# Revit family: ERA_LF_WC_SPB-201
name_source: partatom
category: Осветительные приборы
units: mm (PartAtom-declared; Revit-internal decimal feet)

## family parameters
Всегда вертикально = Да
Заголовок OmniClass = Lighting
Источник света = Да
На основе рабочей плоскости = Нет
Номер OmniClass = 23.80.70.00
Общий = Нет
При загрузке вырезать с полостями = Нет
Размер круглого соединителя = Использовать диаметр
Тип детали = Нормальный
Точка расчета площади = Да

## types (16) — shared parameters
ADSK_Единица измерения = шт.
ADSK_Завод-изготовитель = ЭРА
ADSK_Классификация нагрузок = Освещение
ADSK_Количество фаз = 1
ADSK_Наименование краткое = Светильник
ADSK_Напряжение = 230 В
ADSK_Примечание = Импульсный драйвер
URL = https://www.eraworld.ru
_Корпус_Длина = 1 мм
_Корпус_Ширина = 1 мм
_УГО_Диаметр = 1 мм
_УГО_Длина = 1 мм
_УГО_Ширина = 1 мм
Видимая форма излучения при визуализации = Нет
Геометрия изделия = Круглый
Излучение по длине прямоугольника = 1 мм
Излучение по ширине прямоугольника = 1 мм
Источник света = LED
Класс защиты = II
Класс пожароопасности = Нет
Комплект = Импульсный драйвер
Разработчик модели = https://www.teslabim.ru
Светофильтр = 16777215
Смещение цветовой температуры при затухании лампы = <Нет>
Степень защиты IP = IP65
Тип установки = Настенный
УГО_Масштаб = 100
Угол наклона = 90,00°
Файл фотометрической сетки = SPB-201-0-40K-008.ies
Цвет = Белый
zero-valued in all types: ADSK_Размер_Длина, ADSK_Размер_Ширина

## per-type parameters (varying)
| type | ADSK_Коэффициент мощности | ADSK_Марка | ADSK_Масса | ADSK_Наименование | ADSK_Номинальная мощность | ADSK_Обозначение | ADSK_Полная мощность | ADSK_Размер_Высота | ADSK_Размер_Диаметр | _Корпус_Высота | _Корпус_Диаметр |
| SPB-201-0-40K-008, LED, IP65, d 140х48 мм, 8 Вт, 4000 К, 760 лм, класс защиты II, в комплекте (линейный стабилизатор) | 0.7 | SPB-201-0-40K-008 | 0.118 | Светильник, LED, круглый, настенный, IP65, d 140х48 мм, 8 Вт, 4000 К, 760 лм, класс защиты II, в комплекте (линейный стабилизатор) | 8 Вт | SPB-201-0-40K-008 | 11 В·А | 48 мм | 140 мм | 48 мм | 140 мм |
| SPB-201-0-65K-008, LED, IP65, d 140х48 мм, 8 Вт, 6500 К, 760 лм, класс защиты II, в комплекте (импульсный драйвер) | 0.7 | SPB-201-0-65K-008 | 0.118 | Светильник, LED, круглый, настенный, IP65, d 140х48 мм, 8 Вт, 6500 К, 760 лм, класс защиты II, в комплекте (импульсный драйвер) | 8 Вт | SPB-201-0-65K-008 | 11 В·А | 48 мм | 140 мм | 48 мм | 140 мм |
| SPB-201-1-40K-008, LED, IP65, d 140х48 мм, 8 Вт, 4000 К, 760 лм, класс защиты II, в комплекте (импульсный драйвер) | 0.7 | SPB-201-1-40K-008 | 0.128 | Светильник, LED, круглый, настенный, IP65, d 140х48 мм, 8 Вт, 4000 К, 760 лм, класс защиты II, в комплекте (импульсный драйвер) | 8 Вт | SPB-201-1-40K-008 | 11 В·А | 48 мм | 140 мм | 48 мм | 140 мм |
| SPB-201-1-65K-008, LED, IP65, d 140х48 мм, 8 Вт, 6500 К, 760 лм, класс защиты II, в комплекте (импульсный драйвер) | 0.7 | SPB-201-1-65K-008 | 0.128 | Светильник, LED, круглый, настенный, IP65, d 140х48 мм, 8 Вт, 6500 К, 760 лм, класс защиты II, в комплекте (импульсный драйвер) | 8 Вт | SPB-201-1-65K-008 | 11 В·А | 48 мм | 140 мм | 48 мм | 140 мм |
| SPB-201-2-40K-008, LED, IP65, d 140х48 мм, 8 Вт, 4000 К, 760 лм, класс защиты II, в комплекте (импульсный драйвер) | 0.7 | SPB-201-2-40K-008 | 0.125 | Светильник, LED, круглый, настенный, IP65, d 140х48 мм, 8 Вт, 4000 К, 760 лм, класс защиты II, в комплекте (импульсный драйвер) | 8 Вт | SPB-201-2-40K-008 | 11 В·А | 48 мм | 140 мм | 48 мм | 140 мм |
| SPB-201-2-65K-008, LED, IP65, d 140х48 мм, 8 Вт, 6500 К, 760 лм, класс защиты II, в комплекте (импульсный драйвер) | 0.7 | SPB-201-2-65K-008 | 0.125 | Светильник, LED, круглый, настенный, IP65, d 140х48 мм, 8 Вт, 6500 К, 760 лм, класс защиты II, в комплекте (импульсный драйвер) | 8 Вт | SPB-201-2-65K-008 | 11 В·А | 48 мм | 140 мм | 48 мм | 140 мм |
| SPB-201-0-40K-012, LED, IP65, d 155х52 мм, 12 Вт, 4000 К, 1140 лм, класс защиты II, в комплекте (импульсный драйвер) | 0.85 | SPB-201-0-40K-012 | 0.156 | Светильник, LED, круглый, настенный, IP65, d 155х52 мм, 12 Вт, 4000 К, 1140 лм, класс защиты II, в комплекте (импульсный драйвер) | 12 Вт | SPB-201-0-40K-012 | 14 В·А | 52 мм | 155 мм | 52 мм | 155 мм |
| SPB-201-0-65K-012, LED, IP65, d 155х52 мм, 12 Вт, 6500 К, 1140 лм, класс защиты II, в комплекте (импульсный драйвер) | 0.85 | SPB-201-0-65K-012 | 0.156 | Светильник, LED, круглый, настенный, IP65, d 155х52 мм, 12 Вт, 6500 К, 1140 лм, класс защиты II, в комплекте (импульсный драйвер) | 12 Вт | SPB-201-0-65K-012 | 14 В·А | 52 мм | 155 мм | 52 мм | 155 мм |
| SPB-201-2-40K-012, LED, IP65, d 155х52 мм, 12 Вт, 4000 К, 1140 лм, класс защиты II, в комплекте (импульсный драйвер) | 0.85 | SPB-201-2-40K-012 | 0.162 | Светильник, LED, круглый, настенный, IP65, d 155х52 мм, 12 Вт, 4000 К, 1140 лм, класс защиты II, в комплекте (импульсный драйвер) | 12 Вт | SPB-201-2-40K-012 | 14 В·А | 52 мм | 155 мм | 52 мм | 155 мм |
| SPB-201-2-65K-012, LED, IP65, d 155х52 мм, 12 Вт, 6500 К, 1140 лм, класс защиты II, в комплекте (импульсный драйвер) | 0.85 | SPB-201-2-65K-012 | 0.162 | Светильник, LED, круглый, настенный, IP65, d 155х52 мм, 12 Вт, 6500 К, 1140 лм, класс защиты II, в комплекте (импульсный драйвер) | 12 Вт | SPB-201-2-65K-012 | 14 В·А | 52 мм | 155 мм | 52 мм | 155 мм |
| SPB-201-0-40K-015, LED, IP65, d 175х52 мм, 15 Вт, 4000 К, 1425 лм, класс защиты II, в комплекте (импульсный драйвер) | 0.85 | SPB-201-0-40K-015 | 0.206 | Светильник, LED, круглый, настенный, IP65, d 175х52 мм, 15 Вт, 4000 К, 1425 лм, класс защиты II, в комплекте (импульсный драйвер) | 15 Вт | SPB-201-0-40K-015 | 18 В·А | 52 мм | 175 мм | 52 мм | 175 мм |
| SPB-201-0-65K-015, LED, IP65, d 175х52 мм, 15 Вт, 6500 К, 1425 лм, класс защиты II, в комплекте (импульсный драйвер) | 0.85 | SPB-201-0-65K-015 | 0.206 | Светильник, LED, круглый, настенный, IP65, d 175х52 мм, 15 Вт, 6500 К, 1425 лм, класс защиты II, в комплекте (импульсный драйвер) | 15 Вт | SPB-201-0-65K-015 | 18 В·А | 52 мм | 175 мм | 52 мм | 175 мм |
| SPB-201-1-40K-015, LED, IP65, d 175х52 мм, 15 Вт, 4000 К, 1425 лм, класс защиты II, в комплекте (импульсный драйвер) | 0.85 | SPB-201-1-40K-015 | 0.21 | Светильник, LED, круглый, настенный, IP65, d 175х52 мм, 15 Вт, 4000 К, 1425 лм, класс защиты II, в комплекте (импульсный драйвер) | 15 Вт | SPB-201-1-40K-015 | 18 В·А | 52 мм | 175 мм | 52 мм | 175 мм |
| SPB-201-1-65K-015, LED, IP65, d 175х52 мм, 15 Вт, 6500 К, 1425 лм, класс защиты II, в комплекте (импульсный драйвер) | 0.85 | SPB-201-1-65K-015 | 0.21 | Светильник, LED, круглый, настенный, IP65, d 175х52 мм, 15 Вт, 6500 К, 1425 лм, класс защиты II, в комплекте (импульсный драйвер) | 15 Вт | SPB-201-1-65K-015 | 18 В·А | 52 мм | 175 мм | 52 мм | 175 мм |
| SPB-201-2-40K-015, LED, IP65, d 175х52 мм, 15 Вт, 4000 К, 1425 лм, класс защиты II, в комплекте (импульсный драйвер) | 0.85 | SPB-201-2-40K-015 | 0.215 | Светильник, LED, круглый, настенный, IP65, d 175х52 мм, 15 Вт, 4000 К, 1425 лм, класс защиты II, в комплекте (импульсный драйвер) | 15 Вт | SPB-201-2-40K-015 | 18 В·А | 52 мм | 175 мм | 52 мм | 175 мм |
| SPB-201-2-65K-015, LED, IP65, d 175х52 мм, 15 Вт, 6500 К, 1425 лм, класс защиты II, в комплекте (импульсный драйвер) | 0.85 | SPB-201-2-65K-015 | 0.215 | Светильник, LED, круглый, настенный, IP65, d 175х52 мм, 15 Вт, 6500 К, 1425 лм, класс защиты II, в комплекте (импульсный драйвер) | 15 Вт | SPB-201-2-65K-015 | 18 В·А | 52 мм | 175 мм | 52 мм | 175 мм |
